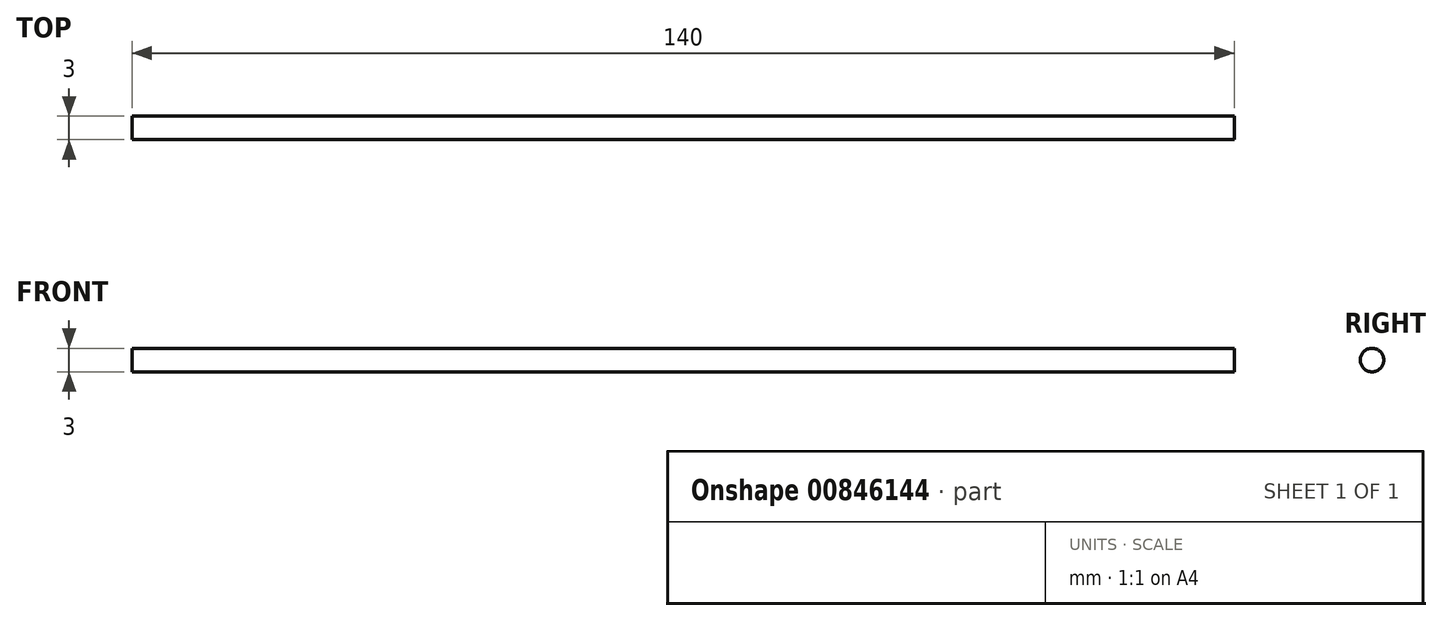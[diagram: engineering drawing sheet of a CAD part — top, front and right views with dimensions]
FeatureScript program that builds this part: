
annotation { "Feature Type Name" : "Feature", "Feature Type Description" : "" }
export const myFeature = defineFeature(function(context is Context, id is Id, definition is map)
    precondition{}
    {
        {
            var Q0;
            Q0=qCreatedBy(makeId("Right.planeOp"),FACE);
            var sketch = newSketch(context, id + "F0", { "sketchPlane" : qUnion([Q0])});
            skCircle(sketch, "E0", {"center": v(0, 0) * mm, "radius": 1.5 * mm});
            skSolve(sketch);
        }
        {
            var Q0;
            Q0=makeQuery(id+"F0.imprint","IMPRINT",FACE,{"disambiguationData":[TD([[makeQuery(id+"F0.imprint","IMPRINT",EDGE,{"derivedFrom":sQuery(id+"F0.wireOp",EDGE,"E0")}),1.0]])]});
            extrude(context, id + "F1", {"entities" : qUnion([Q0]), "depth" : 70 * mm, "offsetDistance" : 25 * mm});
        }
        {
            var Q0;
            Q0=makeQuery(id+"F1.opExtrude","CAP_FACE",FACE,{"disambiguationData":[OSD([sQuery(id+"F0.wireOp",EDGE,"E0")])],"isStart":true});
            var sketch = newSketch(context, id + "F2", { "sketchPlane" : qUnion([Q0])});
            skSolve(sketch);
        }
        {
            var Q0;
            Q0=makeQuery(id+"F2.imprint","IMPRINT",FACE,{"disambiguationData":[TD([[makeQuery(id+"F2.imprint","IMPRINT",EDGE,{"derivedFrom":makeQuery(id+"F1.opExtrude","CAP_EDGE",EDGE,{"disambiguationData":[OSD([sQuery(id+"F0.wireOp",EDGE,"E0")])],"isStart":true})}),-1.0]])]});
            extrude(context, id + "F3", {"entities" : qUnion([Q0]), "operationType" : NewBodyOperationType.ADD, "depth" : 70 * mm, "offsetDistance" : 25 * mm});
        }
    });
